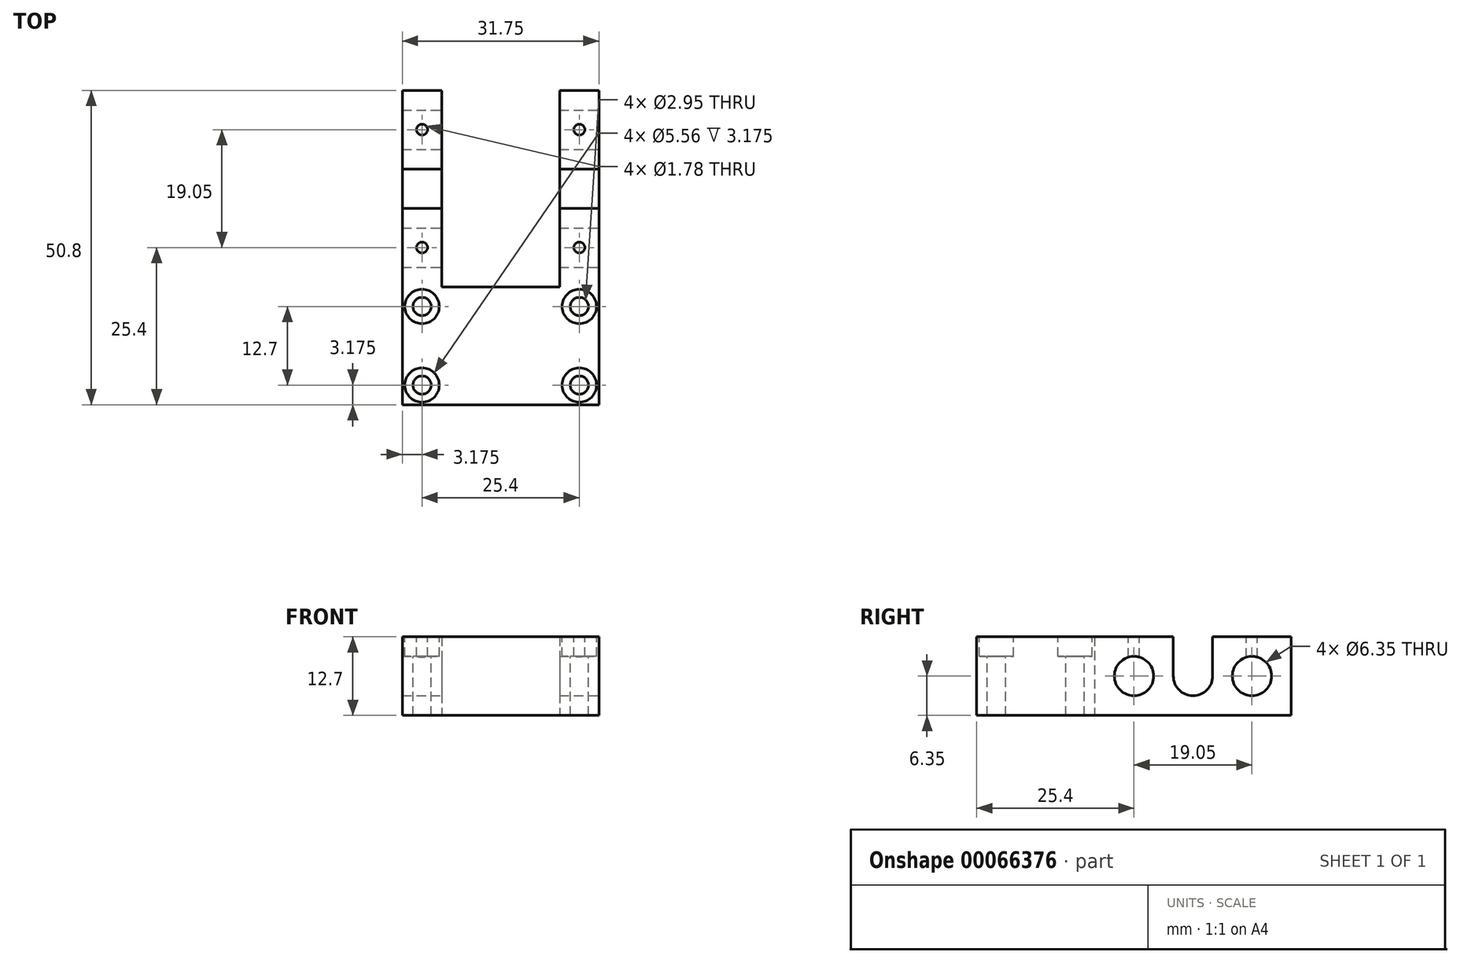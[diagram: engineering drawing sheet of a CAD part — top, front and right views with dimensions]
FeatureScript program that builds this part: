
annotation { "Feature Type Name" : "Feature", "Feature Type Description" : "" }
export const myFeature = defineFeature(function(context is Context, id is Id, definition is map)
    precondition{}
    {
        {
            var Q0;
            Q0=qCreatedBy(makeId("Top.planeOp"),FACE);
            var sketch = newSketch(context, id + "F0", { "sketchPlane" : qUnion([Q0])});
            skLineSegment(sketch, "E0.bottom", {"start": v(0, 0) * mm, "end": v(31.75, 0) * mm});
            skLineSegment(sketch, "E0.top", {"start": v(6.35, 19.05) * mm, "end": v(25.4, 19.05) * mm});
            skLineSegment(sketch, "E0.left", {"start": v(0, 0) * mm, "end": v(0, 19.05) * mm});
            skLineSegment(sketch, "E0.right", {"start": v(31.75, 0) * mm, "end": v(31.75, 19.05) * mm});
            skLineSegment(sketch, "E1.top", {"start": v(0, 50.8) * mm, "end": v(6.35, 50.8) * mm});
            skLineSegment(sketch, "E1.left", {"start": v(0, 19.05) * mm, "end": v(0, 50.8) * mm});
            skLineSegment(sketch, "E1.right", {"start": v(6.35, 19.05) * mm, "end": v(6.35, 50.8) * mm});
            skLineSegment(sketch, "E2.top", {"start": v(31.75, 50.8) * mm, "end": v(25.4, 50.8) * mm});
            skLineSegment(sketch, "E2.left", {"start": v(31.75, 19.05) * mm, "end": v(31.75, 50.8) * mm});
            skLineSegment(sketch, "E2.right", {"start": v(25.4, 19.05) * mm, "end": v(25.4, 50.8) * mm});
            skSolve(sketch);
        }
        {
            var Q0;
            Q0 = qSketchRegion(id + "F0", true);
            extrude(context, id + "F1", {"entities" : qUnion([Q0]), "depth" : 12.7 * mm});
        }
        {
            var Q0;
            Q0=makeQuery(id+"F1.opExtrude","CAP_FACE",FACE,{"disambiguationData":[OSD([sQuery(id+"F0.wireOp",EDGE,"E0.bottom"),sQuery(id+"F0.wireOp",EDGE,"E0.top"),sQuery(id+"F0.wireOp",EDGE,"E0.left"),sQuery(id+"F0.wireOp",EDGE,"E0.right"),sQuery(id+"F0.wireOp",EDGE,"E1.top"),sQuery(id+"F0.wireOp",EDGE,"E1.left"),sQuery(id+"F0.wireOp",EDGE,"E1.right"),sQuery(id+"F0.wireOp",EDGE,"E2.top"),sQuery(id+"F0.wireOp",EDGE,"E2.left"),sQuery(id+"F0.wireOp",EDGE,"E2.right")])],"isStart":false});
            var sketch = newSketch(context, id + "F2", { "sketchPlane" : qUnion([Q0])});
            skPoint(sketch, "E3", {"position": v(3.17, 3.17) * mm});
            skPoint(sketch, "E4", {"position": v(3.17, 15.87) * mm});
            skPoint(sketch, "E5", {"position": v(28.57, 15.87) * mm});
            skPoint(sketch, "E6", {"position": v(28.57, 3.17) * mm});
            skSolve(sketch);
        }
        {
            var Q0;
            Q0=sQuery(id+"F2.wireOp",VERTEX,"E4");
            var Q1;
            Q1=sQuery(id+"F2.wireOp",VERTEX,"E3");
            var Q2;
            Q2=sQuery(id+"F2.wireOp",VERTEX,"E5");
            var Q3;
            Q3=sQuery(id+"F2.wireOp",VERTEX,"E6");
            var Q4;
            Q4=makeQuery(id+"F1.opExtrude","SWEPT_BODY",BODY,{"disambiguationData":[OSD([sQuery(id+"F0.wireOp",EDGE,"E0.bottom"),sQuery(id+"F0.wireOp",EDGE,"E0.top"),sQuery(id+"F0.wireOp",EDGE,"E0.left"),sQuery(id+"F0.wireOp",EDGE,"E0.right"),sQuery(id+"F0.wireOp",EDGE,"E1.top"),sQuery(id+"F0.wireOp",EDGE,"E1.left"),sQuery(id+"F0.wireOp",EDGE,"E1.right"),sQuery(id+"F0.wireOp",EDGE,"E2.top"),sQuery(id+"F0.wireOp",EDGE,"E2.left"),sQuery(id+"F0.wireOp",EDGE,"E2.right")])]});
            hole(context, id + "F3", {"style" : HoleStyle.SIMPLE, "holeDiameter" : 2.95 * mm, "endStyle" : HoleEndStyle.THROUGH, "locations" : qUnion([Q0, Q1, Q2, Q3]), "scope" : qUnion([Q4])});
        }
        {
            var Q0;
            Q0=makeQuery(id+"F1.opExtrude","SWEPT_FACE",FACE,{"disambiguationData":[OSD([sQuery(id+"F0.wireOp",EDGE,"E0.right"),sQuery(id+"F0.wireOp",EDGE,"E2.left")])]});
            var sketch = newSketch(context, id + "F4", { "sketchPlane" : qUnion([Q0])});
            skPoint(sketch, "E7", {"position": v(25.4, 6.35) * mm});
            skPoint(sketch, "E8", {"position": v(44.45, 6.35) * mm});
            skLineSegment(sketch, "E9", {"start": v(0, 6.35) * mm, "end": v(50.8, 6.35) * mm, "construction": true});
            skPoint(sketch, "E10", {"position": v(34.92, 6.35) * mm});
            skSolve(sketch);
        }
        {
            var Q0;
            Q0=sQuery(id+"F4.wireOp",VERTEX,"E7");
            var Q1;
            Q1=sQuery(id+"F4.wireOp",VERTEX,"E8");
            var Q2;
            Q2=sQuery(id+"F4.wireOp",VERTEX,"E10");
            var Q3;
            Q3=makeQuery(id+"F1.opExtrude","SWEPT_BODY",BODY,{"disambiguationData":[OSD([sQuery(id+"F0.wireOp",EDGE,"E0.bottom"),sQuery(id+"F0.wireOp",EDGE,"E0.top"),sQuery(id+"F0.wireOp",EDGE,"E0.left"),sQuery(id+"F0.wireOp",EDGE,"E0.right"),sQuery(id+"F0.wireOp",EDGE,"E1.top"),sQuery(id+"F0.wireOp",EDGE,"E1.left"),sQuery(id+"F0.wireOp",EDGE,"E1.right"),sQuery(id+"F0.wireOp",EDGE,"E2.top"),sQuery(id+"F0.wireOp",EDGE,"E2.left"),sQuery(id+"F0.wireOp",EDGE,"E2.right")])]});
            hole(context, id + "F5", {"style" : HoleStyle.SIMPLE, "holeDiameter" : 6.35 * mm, "endStyle" : HoleEndStyle.THROUGH, "locations" : qUnion([Q0, Q1, Q2]), "scope" : qUnion([Q3])});
        }
        {
            var Q0;
            Q0=makeQuery(id+"F1.opExtrude","SWEPT_FACE",FACE,{"disambiguationData":[OSD([sQuery(id+"F0.wireOp",EDGE,"E0.right"),sQuery(id+"F0.wireOp",EDGE,"E2.left")])]});
            var sketch = newSketch(context, id + "F6", { "sketchPlane" : qUnion([Q0])});
            skLineSegment(sketch, "E11", {"start": v(31.75, 6.35) * mm, "end": v(31.75, 12.7) * mm});
            skLineSegment(sketch, "E12", {"start": v(31.75, 12.7) * mm, "end": v(38.1, 12.7) * mm});
            skLineSegment(sketch, "E13", {"start": v(38.1, 12.7) * mm, "end": v(38.1, 6.35) * mm});
            skLineSegment(sketch, "E14", {"start": v(31.75, 6.35) * mm, "end": v(38.1, 6.35) * mm});
            skSolve(sketch);
        }
        {
            var Q0;
            Q0 = qSketchRegion(id + "F6", true);
            extrude(context, id + "F7", {"entities" : qUnion([Q0]), "operationType" : NewBodyOperationType.REMOVE, "endBound" : BoundingType.THROUGH_ALL, "oppositeDirection" : true, "depth" : 25.4 * mm});
        }
        {
            var Q0;
            Q0 = qSketchRegion(id + "F6", true);
            extrude(context, id + "F8", {"entities" : qUnion([Q0]), "operationType" : NewBodyOperationType.REMOVE, "endBound" : BoundingType.THROUGH_ALL, "oppositeDirection" : true, "depth" : 25.4 * mm});
        }
        {
            var Q0;
            {var subQ0=sQuery(id+"F0.wireOp",EDGE,"E1.left");var subQ1=sQuery(id+"F0.wireOp",EDGE,"E0.left");var subQ2=sQuery(id+"F0.wireOp",EDGE,"E2.right");var subQ3=sQuery(id+"F0.wireOp",EDGE,"E1.right");var subQ4=sQuery(id+"F0.wireOp",EDGE,"E0.bottom");var subQ5=sQuery(id+"F0.wireOp",EDGE,"E0.top");var subQ6=sQuery(id+"F0.wireOp",EDGE,"E2.left");var subQ7=sQuery(id+"F0.wireOp",EDGE,"E0.right");Q0=makeQuery(id+"F7.boolean.opBoolean","SPLIT",FACE,{"disambiguationData":[TD([makeQuery(id+"F1.opExtrude","SWEPT_FACE",FACE,{"disambiguationData":[OSD([subQ4])]})])],"derivedFrom":makeQuery(id+"F1.opExtrude","CAP_FACE",FACE,{"disambiguationData":[OSD([subQ4,subQ5,subQ1,subQ7,sQuery(id+"F0.wireOp",EDGE,"E1.top"),subQ0,subQ3,sQuery(id+"F0.wireOp",EDGE,"E2.top"),subQ6,subQ2])],"isStart":false})});}
            var sketch = newSketch(context, id + "F9", { "sketchPlane" : qUnion([Q0])});
            skCircle(sketch, "E15", {"center": v(3.17, 3.17) * mm, "radius": 2.78 * mm});
            skCircle(sketch, "E16", {"center": v(3.17, 15.87) * mm, "radius": 2.78 * mm});
            skCircle(sketch, "E17", {"center": v(28.57, 3.17) * mm, "radius": 2.78 * mm});
            skCircle(sketch, "E18", {"center": v(28.57, 15.87) * mm, "radius": 2.78 * mm});
            skSolve(sketch);
        }
        {
            var Q0;
            Q0 = qSketchRegion(id + "F9", true);
            extrude(context, id + "F10", {"entities" : qUnion([Q0]), "operationType" : NewBodyOperationType.REMOVE, "oppositeDirection" : true, "depth" : 3.17 * mm});
        }
        {
            var Q0;
            {var subQ0=sQuery(id+"F0.wireOp",EDGE,"E2.left");var subQ1=sQuery(id+"F0.wireOp",EDGE,"E0.right");var subQ2=sQuery(id+"F0.wireOp",EDGE,"E2.top");var subQ3=sQuery(id+"F0.wireOp",EDGE,"E2.right");Q0=makeQuery(id+"F7.boolean.opBoolean","SPLIT",FACE,{"disambiguationData":[TD([makeQuery(id+"F1.opExtrude","SWEPT_FACE",FACE,{"disambiguationData":[OSD([subQ2])]})])],"derivedFrom":makeQuery(id+"F1.opExtrude","CAP_FACE",FACE,{"disambiguationData":[OSD([sQuery(id+"F0.wireOp",EDGE,"E0.bottom"),sQuery(id+"F0.wireOp",EDGE,"E0.top"),sQuery(id+"F0.wireOp",EDGE,"E0.left"),subQ1,sQuery(id+"F0.wireOp",EDGE,"E1.top"),sQuery(id+"F0.wireOp",EDGE,"E1.left"),sQuery(id+"F0.wireOp",EDGE,"E1.right"),subQ2,subQ0,subQ3])],"isStart":false})});}
            var sketch = newSketch(context, id + "F11", { "sketchPlane" : qUnion([Q0])});
            skLineSegment(sketch, "E19", {"start": v(28.57, 50.8) * mm, "end": v(28.57, 0) * mm, "construction": true});
            skPoint(sketch, "E20", {"position": v(28.57, 44.45) * mm});
            skPoint(sketch, "E21", {"position": v(28.57, 25.4) * mm});
            skSolve(sketch);
        }
        {
            var Q0;
            {var subQ0=sQuery(id+"F0.wireOp",EDGE,"E1.left");var subQ1=sQuery(id+"F0.wireOp",EDGE,"E0.left");var subQ2=sQuery(id+"F0.wireOp",EDGE,"E1.top");var subQ3=sQuery(id+"F0.wireOp",EDGE,"E1.right");Q0=makeQuery(id+"F7.boolean.opBoolean","SPLIT",FACE,{"disambiguationData":[TD([makeQuery(id+"F1.opExtrude","SWEPT_FACE",FACE,{"disambiguationData":[OSD([subQ2])]})])],"derivedFrom":makeQuery(id+"F1.opExtrude","CAP_FACE",FACE,{"disambiguationData":[OSD([sQuery(id+"F0.wireOp",EDGE,"E0.bottom"),sQuery(id+"F0.wireOp",EDGE,"E0.top"),subQ1,sQuery(id+"F0.wireOp",EDGE,"E0.right"),subQ2,subQ0,subQ3,sQuery(id+"F0.wireOp",EDGE,"E2.top"),sQuery(id+"F0.wireOp",EDGE,"E2.left"),sQuery(id+"F0.wireOp",EDGE,"E2.right")])],"isStart":false})});}
            var sketch = newSketch(context, id + "F12", { "sketchPlane" : qUnion([Q0])});
            skLineSegment(sketch, "E22", {"start": v(3.17, 50.8) * mm, "end": v(3.17, 0) * mm, "construction": true});
            skPoint(sketch, "E23", {"position": v(3.17, 44.45) * mm});
            skPoint(sketch, "E24", {"position": v(3.17, 25.4) * mm});
            skSolve(sketch);
        }
        {
            var Q0;
            Q0=sQuery(id+"F12.wireOp",VERTEX,"E24");
            var Q1;
            Q1=sQuery(id+"F12.wireOp",VERTEX,"E23");
            var Q2;
            Q2=sQuery(id+"F11.wireOp",VERTEX,"E21");
            var Q3;
            Q3=sQuery(id+"F11.wireOp",VERTEX,"E20");
            var Q4;
            Q4=makeQuery(id+"F1.opExtrude","SWEPT_BODY",BODY,{"disambiguationData":[OSD([sQuery(id+"F0.wireOp",EDGE,"E0.bottom"),sQuery(id+"F0.wireOp",EDGE,"E0.top"),sQuery(id+"F0.wireOp",EDGE,"E0.left"),sQuery(id+"F0.wireOp",EDGE,"E0.right"),sQuery(id+"F0.wireOp",EDGE,"E1.top"),sQuery(id+"F0.wireOp",EDGE,"E1.left"),sQuery(id+"F0.wireOp",EDGE,"E1.right"),sQuery(id+"F0.wireOp",EDGE,"E2.top"),sQuery(id+"F0.wireOp",EDGE,"E2.left"),sQuery(id+"F0.wireOp",EDGE,"E2.right")])]});
            hole(context, id + "F13", {"style" : HoleStyle.SIMPLE, "holeDiameter" : 1.78 * mm, "endStyle" : HoleEndStyle.BLIND, "holeDepth" : 6.35 * mm, "locations" : qUnion([Q0, Q1, Q2, Q3]), "scope" : qUnion([Q4])});
        }
    });
